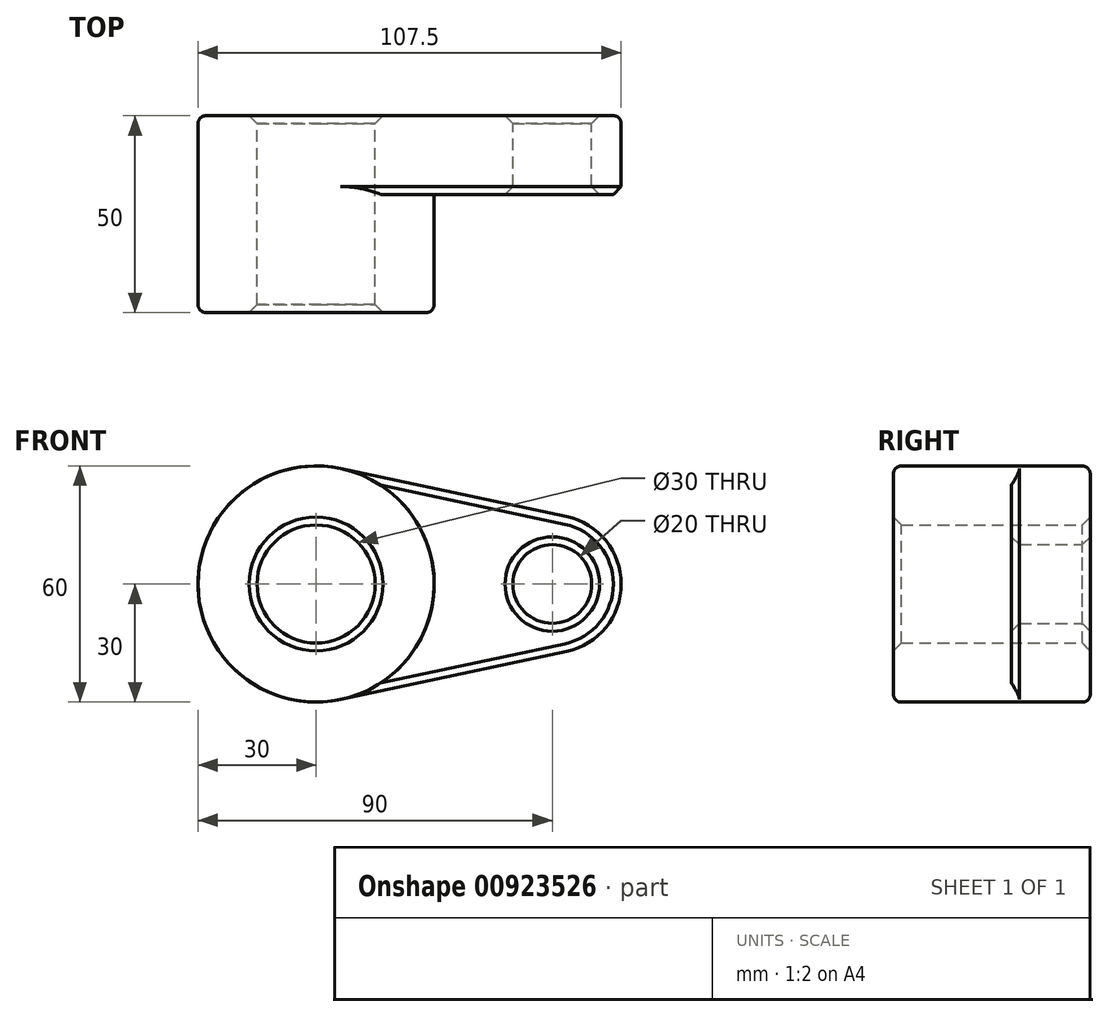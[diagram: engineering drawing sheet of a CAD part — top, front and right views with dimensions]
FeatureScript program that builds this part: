
annotation { "Feature Type Name" : "Feature", "Feature Type Description" : "" }
export const myFeature = defineFeature(function(context is Context, id is Id, definition is map)
    precondition{}
    {
        {
            var Q0;
            Q0=qCreatedBy(makeId("Front.planeOp"),FACE);
            var sketch = newSketch(context, id + "F0", { "sketchPlane" : qUnion([Q0])});
            skCircle(sketch, "E0", {"center": v(0, 0) * mm, "radius": 30 * mm});
            skCircle(sketch, "E1", {"center": v(60, 0) * mm, "radius": 17.5 * mm});
            skCircle(sketch, "E2", {"center": v(0, 0) * mm, "radius": 15 * mm});
            skCircle(sketch, "E3", {"center": v(60, 0) * mm, "radius": 10 * mm});
            skLineSegment(sketch, "E4", {"start": v(6.25, -29.34) * mm, "end": v(63.65, -17.12) * mm});
            skLineSegment(sketch, "E5", {"start": v(6.25, 29.34) * mm, "end": v(63.65, 17.12) * mm});
            skSolve(sketch);
        }
        {
            var Q0;
            Q0 = qSketchRegion(id + "F0", true);
            extrude(context, id + "F1", {"entities" : qUnion([Q0]), "depth" : 20 * mm, "offsetDistance" : 25 * mm});
        }
        {
            var Q0;
            Q0=makeQuery(id+"F0.imprint","IMPRINT",FACE,{"disambiguationData":[TD([[makeQuery(id+"F0.imprint","IMPRINT",EDGE,{"derivedFrom":sQuery(id+"F0.wireOp",EDGE,"E2")}),-1.0]])]});
            extrude(context, id + "F2", {"entities" : qUnion([Q0]), "operationType" : NewBodyOperationType.ADD, "depth" : 50 * mm, "offsetDistance" : 25 * mm});
        }
        {
            var Q0;
            Q0=makeQuery(id+"F2.opExtrude","CAP_EDGE",EDGE,{"disambiguationData":[OSD([sQuery(id+"F0.wireOp",EDGE,"E0")])],"isStart":false});
            var Q1;
            Q1=makeQuery(id+"F1.opExtrude","CAP_EDGE",EDGE,{"disambiguationData":[OSD([sQuery(id+"F0.wireOp",EDGE,"E4")])],"isStart":true});
            fillet(context, id + "F3", {"entities" : qUnion([Q0, Q1]), "radius" : 2 * mm, "tangentPropagation" : true, "allowEdgeOverflow" : false});
        }
        {
            var Q0;
            {var subQ0=sQuery(id+"F0.wireOp",EDGE,"E2");Q0=makeQuery(id+"F2.boolean.opBoolean","MERGE",FACE,{"derivedFrom":[makeQuery(id+"F1.opExtrude","SWEPT_FACE",FACE,{"disambiguationData":[OSD([subQ0])]}),makeQuery(id+"F2.opExtrude","SWEPT_FACE",FACE,{"disambiguationData":[OSD([subQ0])]})]});}
            var Q1;
            Q1=makeQuery(id+"F1.opExtrude","CAP_EDGE",EDGE,{"disambiguationData":[OSD([sQuery(id+"F0.wireOp",EDGE,"E3")])],"isStart":false});
            var Q2;
            Q2=makeQuery(id+"F1.opExtrude","CAP_EDGE",EDGE,{"disambiguationData":[OSD([sQuery(id+"F0.wireOp",EDGE,"E1")])],"isStart":false});
            var Q3;
            Q3=makeQuery(id+"F1.opExtrude","CAP_EDGE",EDGE,{"disambiguationData":[OSD([sQuery(id+"F0.wireOp",EDGE,"E3")])],"isStart":true});
            var Q4;
            {var subQ0=sQuery(id+"F0.wireOp",EDGE,"E1");Q4=makeQuery(id+"F3.opFillet","BLEND_EDGE",EDGE,{"blendedFrom":[makeQuery(id+"F1.opExtrude","CAP_EDGE",EDGE,{"disambiguationData":[OSD([subQ0])],"isStart":true}),makeQuery(id+"F1.opExtrude","SWEPT_FACE",FACE,{"disambiguationData":[OSD([subQ0])]})],"blendedInto":[makeQuery(id+"F1.opExtrude","SWEPT_FACE",FACE,{"disambiguationData":[OSD([subQ0])]})]});}
            var Q5;
            {var subQ0=sQuery(id+"F0.wireOp",EDGE,"E1");Q5=makeQuery(id+"F3.opFillet","BLEND_EDGE",EDGE,{"blendedFrom":[makeQuery(id+"F1.opExtrude","CAP_EDGE",EDGE,{"disambiguationData":[OSD([subQ0])],"isStart":true}),makeQuery(id+"F1.opExtrude","CAP_FACE",FACE,{"disambiguationData":[OSD([sQuery(id+"F0.wireOp",EDGE,"E0"),subQ0,sQuery(id+"F0.wireOp",EDGE,"E2"),sQuery(id+"F0.wireOp",EDGE,"E3"),sQuery(id+"F0.wireOp",EDGE,"E4"),sQuery(id+"F0.wireOp",EDGE,"E5")])],"isStart":true})],"blendedInto":[makeQuery(id+"F1.opExtrude","CAP_FACE",FACE,{"disambiguationData":[OSD([sQuery(id+"F0.wireOp",EDGE,"E0"),subQ0,sQuery(id+"F0.wireOp",EDGE,"E2"),sQuery(id+"F0.wireOp",EDGE,"E3"),sQuery(id+"F0.wireOp",EDGE,"E4"),sQuery(id+"F0.wireOp",EDGE,"E5")])],"isStart":true})]});}
            var Q6;
            Q6=makeQuery(id+"F1.opExtrude","SWEPT_EDGE",EDGE,{"disambiguationData":[OSD([sQuery(id+"F0.wireOp",EDGE,"E1"),sQuery(id+"F0.wireOp",EDGE,"E4")])]});
            var Q7;
            Q7=makeQuery(id+"F3.opFillet","BLEND_EDGE",EDGE,{"blendedFrom":[makeQuery(id+"F1.opExtrude","CAP_EDGE",EDGE,{"disambiguationData":[OSD([sQuery(id+"F0.wireOp",EDGE,"E1")])],"isStart":true}),makeQuery(id+"F1.opExtrude","CAP_EDGE",EDGE,{"disambiguationData":[OSD([sQuery(id+"F0.wireOp",EDGE,"E4")])],"isStart":true})],"blendedInto":[]});
            var Q8;
            {var subQ0=sQuery(id+"F0.wireOp",EDGE,"E4");Q8=makeQuery(id+"F3.opFillet","BLEND_EDGE",EDGE,{"blendedFrom":[makeQuery(id+"F1.opExtrude","CAP_EDGE",EDGE,{"disambiguationData":[OSD([subQ0])],"isStart":true}),makeQuery(id+"F1.opExtrude","SWEPT_FACE",FACE,{"disambiguationData":[OSD([subQ0])]})],"blendedInto":[makeQuery(id+"F1.opExtrude","SWEPT_FACE",FACE,{"disambiguationData":[OSD([subQ0])]})]});}
            var Q9;
            {var subQ0=sQuery(id+"F0.wireOp",EDGE,"E4");Q9=makeQuery(id+"F3.opFillet","BLEND_EDGE",EDGE,{"blendedFrom":[makeQuery(id+"F1.opExtrude","CAP_EDGE",EDGE,{"disambiguationData":[OSD([subQ0])],"isStart":true}),makeQuery(id+"F1.opExtrude","CAP_FACE",FACE,{"disambiguationData":[OSD([sQuery(id+"F0.wireOp",EDGE,"E0"),sQuery(id+"F0.wireOp",EDGE,"E1"),sQuery(id+"F0.wireOp",EDGE,"E2"),sQuery(id+"F0.wireOp",EDGE,"E3"),subQ0,sQuery(id+"F0.wireOp",EDGE,"E5")])],"isStart":true})],"blendedInto":[makeQuery(id+"F1.opExtrude","CAP_FACE",FACE,{"disambiguationData":[OSD([sQuery(id+"F0.wireOp",EDGE,"E0"),sQuery(id+"F0.wireOp",EDGE,"E1"),sQuery(id+"F0.wireOp",EDGE,"E2"),sQuery(id+"F0.wireOp",EDGE,"E3"),subQ0,sQuery(id+"F0.wireOp",EDGE,"E5")])],"isStart":true})]});}
            chamfer(context, id + "F4", {"entities" : qUnion([Q0, Q1, Q2, Q3, Q4, Q5, Q6, Q7, Q8, Q9]), "width" : 2 * mm, "tangentPropagation" : true});
        }
    });
